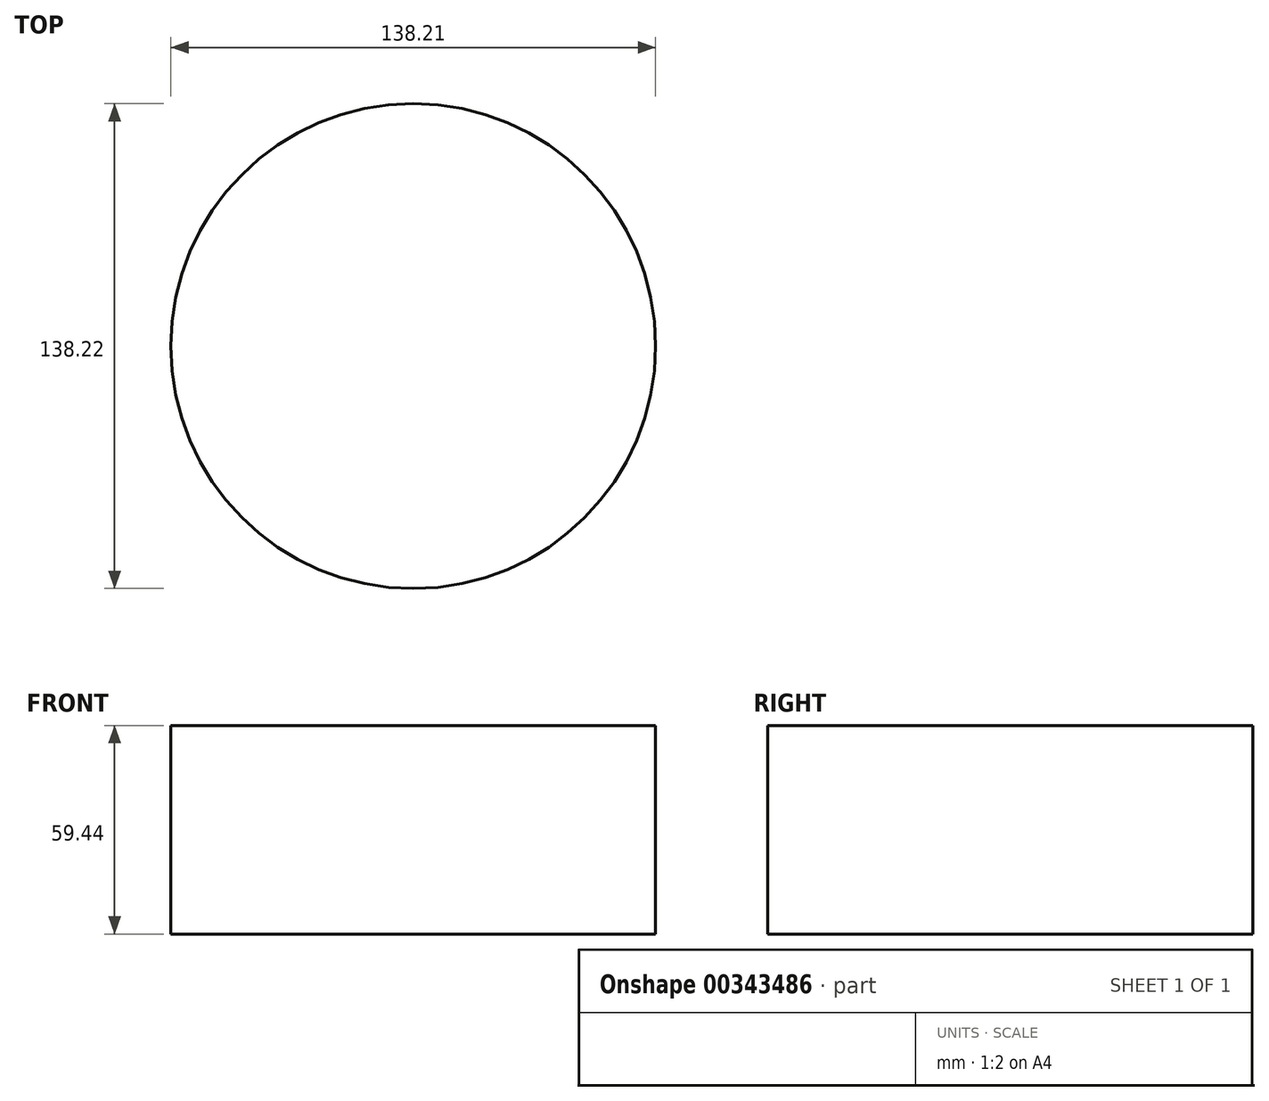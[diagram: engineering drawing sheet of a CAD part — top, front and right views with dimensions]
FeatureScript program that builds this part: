
annotation { "Feature Type Name" : "Feature", "Feature Type Description" : "" }
export const myFeature = defineFeature(function(context is Context, id is Id, definition is map)
    precondition{}
    {
        {
            var Q0;
            Q0=qCreatedBy(makeId("Top.planeOp"),FACE);
            var sketch = newSketch(context, id + "F0", { "sketchPlane" : qUnion([Q0])});
            skCircle(sketch, "E0", {"center": v(-80.82, 13.26) * mm, "radius": 69.1 * mm});
            skSolve(sketch);
        }
        {
            var Q0;
            Q0=makeQuery(id+"F0.imprint","IMPRINT",FACE,{"disambiguationData":[TD([[makeQuery(id+"F0.imprint","IMPRINT",EDGE,{"derivedFrom":sQuery(id+"F0.wireOp",EDGE,"E0")}),1.0]])]});
            extrude(context, id + "F1", {"entities" : qUnion([Q0]), "depth" : 59.44 * mm});
        }
    });
